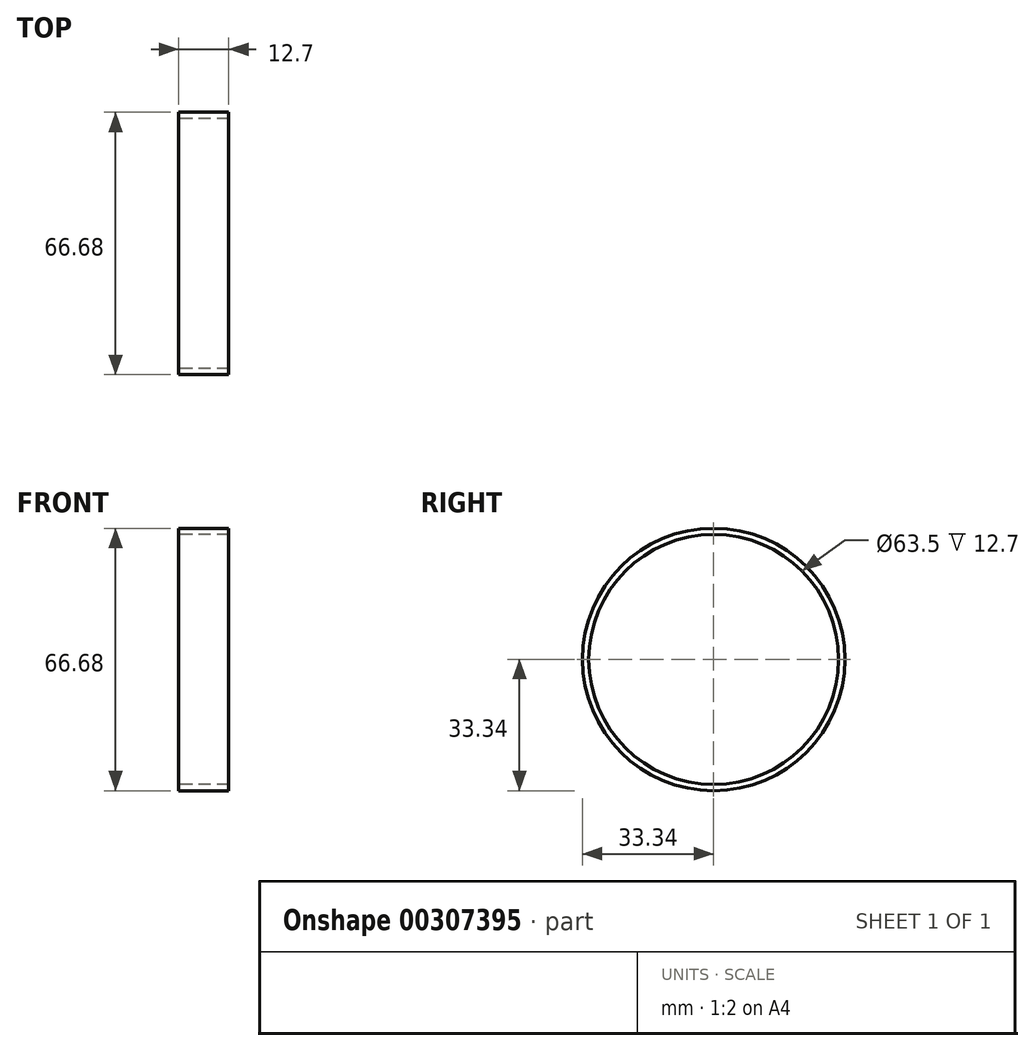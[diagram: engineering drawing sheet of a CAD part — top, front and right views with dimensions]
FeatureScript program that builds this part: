
annotation { "Feature Type Name" : "Feature", "Feature Type Description" : "" }
export const myFeature = defineFeature(function(context is Context, id is Id, definition is map)
    precondition{}
    {
        {
            var Q0;
            Q0=qCreatedBy(makeId("Right.planeOp"),FACE);
            var sketch = newSketch(context, id + "F0", { "sketchPlane" : qUnion([Q0])});
            skCircle(sketch, "E0", {"center": v(0, 0) * mm, "radius": 33.34 * mm});
            skCircle(sketch, "E1", {"center": v(0, 0) * mm, "radius": 31.75 * mm});
            skSolve(sketch);
        }
        {
            var Q0;
            Q0 = qSketchRegion(id + "F0", true);
            extrude(context, id + "F1", {"entities" : qUnion([Q0]), "endBound" : BoundingType.SYMMETRIC, "depth" : 12.7 * mm});
        }
    });
